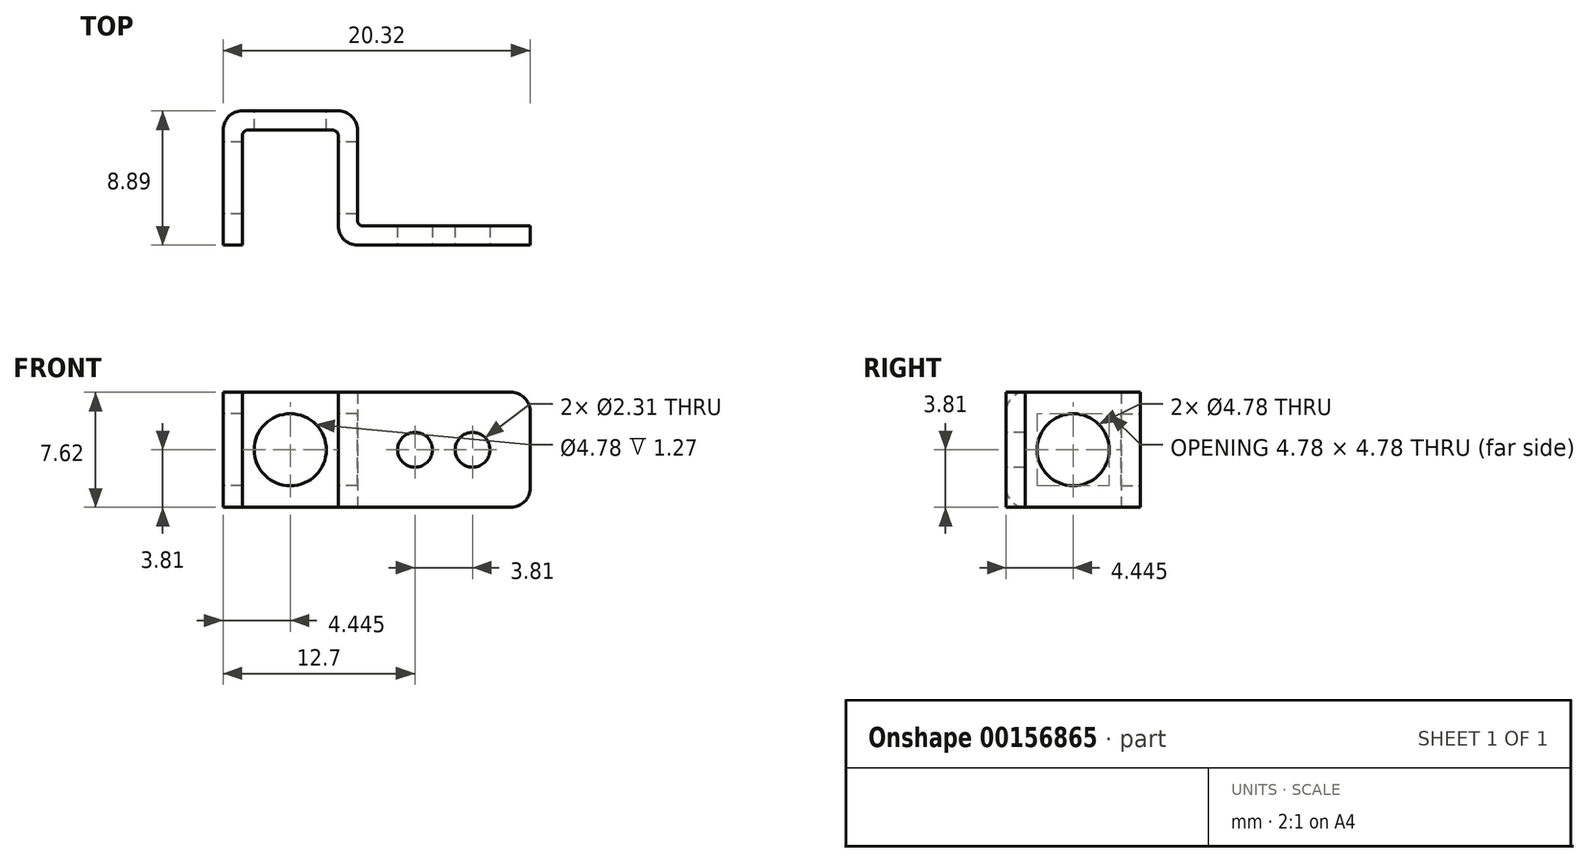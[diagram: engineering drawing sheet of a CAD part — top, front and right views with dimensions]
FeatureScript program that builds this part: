
annotation { "Feature Type Name" : "Feature", "Feature Type Description" : "" }
export const myFeature = defineFeature(function(context is Context, id is Id, definition is map)
    precondition{}
    {
        {
            var Q0;
            Q0=qCreatedBy(makeId("Top.planeOp"),FACE);
            var sketch = newSketch(context, id + "F0", { "sketchPlane" : qUnion([Q0])});
            skLineSegment(sketch, "E0", {"start": v(-8.9, 0) * mm, "end": v(-8.9, 8.9) * mm});
            skLineSegment(sketch, "E1", {"start": v(-8.9, 8.9) * mm, "end": v(0, 8.9) * mm});
            skLineSegment(sketch, "E2", {"start": v(0, 8.9) * mm, "end": v(0, 1.27) * mm});
            skLineSegment(sketch, "E3", {"start": v(0, 1.27) * mm, "end": v(11.43, 1.27) * mm});
            skLineSegment(sketch, "E4", {"start": v(11.43, 1.27) * mm, "end": v(11.43, 0) * mm});
            skLineSegment(sketch, "E5", {"start": v(11.43, 0) * mm, "end": v(-1.27, 0) * mm});
            skLineSegment(sketch, "E6", {"start": v(-1.27, 0) * mm, "end": v(-1.27, 7.62) * mm});
            skLineSegment(sketch, "E7", {"start": v(-1.27, 7.62) * mm, "end": v(-7.62, 7.62) * mm});
            skLineSegment(sketch, "E8", {"start": v(-7.62, 7.62) * mm, "end": v(-7.62, 0) * mm});
            skLineSegment(sketch, "E9", {"start": v(-7.62, 0) * mm, "end": v(-8.9, 0) * mm});
            skSolve(sketch);
        }
        {
            var Q0;
            Q0=makeQuery(id+"F0.imprint","IMPRINT",FACE,{"disambiguationData":[TD([[makeQuery(id+"F0.imprint","IMPRINT",EDGE,{"derivedFrom":sQuery(id+"F0.wireOp",EDGE,"E0")}),-1.0]])]});
            extrude(context, id + "F1", {"entities" : qUnion([Q0]), "endBound" : BoundingType.SYMMETRIC, "depth" : 7.62 * mm});
        }
        {
            var Q0;
            Q0=makeQuery(id+"F1.opExtrude","SWEPT_FACE",FACE,{"disambiguationData":[OSD([sQuery(id+"F0.wireOp",EDGE,"E5")])]});
            var sketch = newSketch(context, id + "F2", { "sketchPlane" : qUnion([Q0])});
            skCircle(sketch, "E10", {"center": v(3.81, 0) * mm, "radius": 1.16 * mm});
            skCircle(sketch, "E11", {"center": v(7.62, 0) * mm, "radius": 1.16 * mm});
            skSolve(sketch);
        }
        {
            var Q0;
            Q0=makeQuery(id+"F1.opExtrude","CAP_EDGE",EDGE,{"disambiguationData":[OSD([sQuery(id+"F0.wireOp",EDGE,"E4")])],"isStart":false});
            var Q1;
            Q1=makeQuery(id+"F1.opExtrude","CAP_EDGE",EDGE,{"disambiguationData":[OSD([sQuery(id+"F0.wireOp",EDGE,"E4")])],"isStart":true});
            var Q2;
            Q2=makeQuery(id+"F1.opExtrude","CAP_EDGE",EDGE,{"disambiguationData":[OSD([sQuery(id+"F0.wireOp",EDGE,"E9")])],"isStart":false});
            var Q3;
            Q3=makeQuery(id+"F1.opExtrude","CAP_EDGE",EDGE,{"disambiguationData":[OSD([sQuery(id+"F0.wireOp",EDGE,"E9")])],"isStart":true});
            var Q4;
            Q4=makeQuery(id+"F1.opExtrude","SWEPT_EDGE",EDGE,{"disambiguationData":[OSD([sQuery(id+"F0.wireOp",EDGE,"E5"),sQuery(id+"F0.wireOp",EDGE,"E6")])]});
            var Q5;
            Q5=makeQuery(id+"F1.opExtrude","SWEPT_EDGE",EDGE,{"disambiguationData":[OSD([sQuery(id+"F0.wireOp",EDGE,"E1"),sQuery(id+"F0.wireOp",EDGE,"E2")])]});
            var Q6;
            Q6=makeQuery(id+"F1.opExtrude","SWEPT_EDGE",EDGE,{"disambiguationData":[OSD([sQuery(id+"F0.wireOp",EDGE,"E0"),sQuery(id+"F0.wireOp",EDGE,"E1")])]});
            fillet(context, id + "F3", {"entities" : qUnion([Q0, Q1, Q2, Q3, Q4, Q5, Q6]), "radius" : 1.27 * mm, "allowEdgeOverflow" : false});
        }
        {
            var Q0;
            Q0=makeQuery(id+"F1.opExtrude","SWEPT_EDGE",EDGE,{"disambiguationData":[OSD([sQuery(id+"F0.wireOp",EDGE,"E7"),sQuery(id+"F0.wireOp",EDGE,"E8")])]});
            var Q1;
            Q1=makeQuery(id+"F1.opExtrude","SWEPT_EDGE",EDGE,{"disambiguationData":[OSD([sQuery(id+"F0.wireOp",EDGE,"E6"),sQuery(id+"F0.wireOp",EDGE,"E7")])]});
            var Q2;
            Q2=makeQuery(id+"F1.opExtrude","SWEPT_EDGE",EDGE,{"disambiguationData":[OSD([sQuery(id+"F0.wireOp",EDGE,"E2"),sQuery(id+"F0.wireOp",EDGE,"E3")])]});
            fillet(context, id + "F4", {"entities" : qUnion([Q0, Q1, Q2]), "radius" : 0.38 * mm, "tangentPropagation" : true, "allowEdgeOverflow" : false});
        }
        {
            var Q0;
            Q0=sQuery(id+"F2.wireOp",VERTEX,"E11.center");
            var Q1;
            Q1=sQuery(id+"F2.wireOp",VERTEX,"E10.center");
            var Q2;
            Q2=makeQuery(id+"F1.opExtrude","SWEPT_BODY",BODY,{"disambiguationData":[OSD([sQuery(id+"F0.wireOp",EDGE,"E0"),sQuery(id+"F0.wireOp",EDGE,"E1"),sQuery(id+"F0.wireOp",EDGE,"E2"),sQuery(id+"F0.wireOp",EDGE,"E3"),sQuery(id+"F0.wireOp",EDGE,"E4"),sQuery(id+"F0.wireOp",EDGE,"E5"),sQuery(id+"F0.wireOp",EDGE,"E6"),sQuery(id+"F0.wireOp",EDGE,"E7"),sQuery(id+"F0.wireOp",EDGE,"E8"),sQuery(id+"F0.wireOp",EDGE,"E9")])]});
            hole(context, id + "F5", {"style" : HoleStyle.SIMPLE, "endStyle" : HoleEndStyle.THROUGH, "holeDiameter" : 2.31 * mm, "locations" : qUnion([Q0, Q1]), "scope" : qUnion([Q2]), "isTappedThrough" : true});
        }
        {
            var Q0;
            Q0=makeQuery(id+"F1.opExtrude","SWEPT_FACE",FACE,{"disambiguationData":[OSD([sQuery(id+"F0.wireOp",EDGE,"E0")])]});
            var sketch = newSketch(context, id + "F6", { "sketchPlane" : qUnion([Q0])});
            skCircle(sketch, "E12", {"center": v(-4.45, 0) * mm, "radius": 2.39 * mm});
            skSolve(sketch);
        }
        {
            var Q0;
            Q0=makeQuery(id+"F6.imprint","IMPRINT",FACE,{"disambiguationData":[TD([[makeQuery(id+"F6.imprint","IMPRINT",EDGE,{"derivedFrom":sQuery(id+"F6.wireOp",EDGE,"E12")}),1.0]])]});
            extrude(context, id + "F7", {"entities" : qUnion([Q0]), "operationType" : NewBodyOperationType.REMOVE, "oppositeDirection" : true, "depth" : 25.4 * mm});
        }
        {
            var Q0;
            Q0=makeQuery(id+"F1.opExtrude","SWEPT_FACE",FACE,{"disambiguationData":[OSD([sQuery(id+"F0.wireOp",EDGE,"E1")])]});
            var sketch = newSketch(context, id + "F8", { "sketchPlane" : qUnion([Q0])});
            skCircle(sketch, "E13", {"center": v(4.45, 0) * mm, "radius": 2.39 * mm});
            skSolve(sketch);
        }
        {
            var Q0;
            Q0=makeQuery(id+"F8.imprint","IMPRINT",FACE,{"disambiguationData":[TD([[makeQuery(id+"F8.imprint","IMPRINT",EDGE,{"derivedFrom":sQuery(id+"F8.wireOp",EDGE,"E13")}),1.0]])]});
            extrude(context, id + "F9", {"entities" : qUnion([Q0]), "operationType" : NewBodyOperationType.REMOVE, "oppositeDirection" : true, "depth" : 25.4 * mm});
        }
    });
